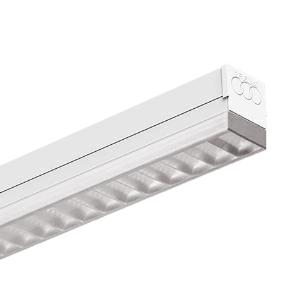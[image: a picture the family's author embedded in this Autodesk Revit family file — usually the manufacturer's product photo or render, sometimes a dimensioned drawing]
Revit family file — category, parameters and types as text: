
# Revit family: 3f_filippi_-_3f_linux_dr_ugr_3f_filippi_-_a20600_-_3f_linux_dr_2x22_led_dali_ugr_l1778
name_source: partatom
category: Lighting Fixtures
units: mm (PartAtom-declared; Revit-internal decimal feet)

## family parameters
Cut with Voids When Loaded = No
Host = Face
Light Source = No
Part Type = Normal
Room Calculation Point = No
Round Connector Dimension = Use Diameter
Shared = No

## types (1)
- 3F Filippi - 3F Linux DR UGR (1 x LED, 5361 lm, 49 W, 4000 K)
    Apparent Load = 49 VA
    Approval mark = CE
    CIE Flux Codes = 71 97 100 99 100
    Color Rendering = 80
    Color Temperature = 4000 K
    Control Gear = Electronic transformer
    Default Elevation = 1800 mm
    Description = Light unit for structure continues 3F Linux S.

ILLUMINOTECHNICAL
Luminous efficiency 100% (DLOR 99%, ULOR 1%).
Initial luminous flux of the luminaire 5361 lm.
Direct symmetric distribution.
Installation Interdistance Transv.D = 1.24 x hu - Long.D = 1.17 x hu.
Average luminance <3000 cd/m² for radial angles >65°.
Tabular UGR (CIE 117 - 4H-8H; S=0.25H; 70/50/20): RUG 17.8 - 19.
Beam angle: 87° - 90°.
Luminous efficacy 109 lm/W.
Lifetime (L93/B10): 30000 h. (tq+25°C)
Lifetime (L90/B10): 50000 h. (tq+25°C)
Lifetime (L85/B10): 80000 h. (tq+25°C)
Lifetime (L80/B10): 100000 h. (tq+25°C)
Sudden decreased luminous flux after 50000 hours: 0% (C0).
Photobiological safety in compliance with IEC/TR 62778: RG0 risk exempt, (IEC 62471).
In compliance with IEC/EN 62722-2-1 - IEC/EN 62717 standards.

SOURCE
2 linear LED modules 22W/840.
Energy efficiency class (UE 2019/2020 - UE 2019/2015): D.
CIE 13.3 Colour rendering index: CRI >80 (R9 <50%).
IES TM-30 Fidelity Index: Rf = 84 Rg = 95.
CCT nominal colour temperature 4000 K.
Colour initial tolerance (MacAdam): SDCM 3.

MECHANICAL
Light unit in hot-galvanised steel, painted in white polyester base with fixing springs and retractable safety hooks in stainless steel.
Rectangular screen in self-extinguishing polycarbonate, UV stabilised, transparent, with smooth outer surface.
Semi-specular aluminium internal louvre with prismatic methacrylate (PMMA) filter above the louvre blades for complete shielding of the louvre compartment.
Luminaire with limited surface temperature. - D - (EN 60598-2-24)
Dimensions: 1778x62 mm, height 81 mm. Weight 2.965 kg.
IP40 protection degree.
Mechanical strength to impacts IK06 (1 joule).
Glow-wire test resistance 850°C.

ELECTRICAL
Halogen Free DALI-2 DATI (Parts 251, 252, 253), PUSH-DIM, electronic wiring 230V-50/60Hz, power factor 0.95 at full load, THD <25%, constant output current, SELV, class I, 1 driver, 1 DALI addresse.
Power of the luminaire 49 W.
ENEC - CE.
SAFE FLICKER: PstLM=<1 and SVM=<0.4 (IEC TR 61547-1 and IEC TR 63158), to ensure a more comfortable and safe light.
Luminaire compliant with EN 60598-2-22 for power supply from a centralised emergency system CPSS (Central Power Supply System), not incorporated in the luminaire - high risk areas excluded. The default power and flux are 100% in AC and 15% in DC.
Ambient temperature from 0°C to +35°C.
Temperature class T6 max 85°C.
Connection to the structure with 3-pin plug with phase selection (H05Z-U Halogen Free cable section 0.5 mm² HT90).
Relative humidity UR: <85%.

INSTALLATION
Ceiling / Suspended / Wall.
All accessories dedicated to this product are available on the Catalog and on our website www.3F-Filippi.com.

STRUCTURE
Hot-galvanised wired structure, painted in polyester base white, obtained through rolling process.
Saline-mist resistance equal to 300hrs and damp resistance equal to 700hrs.
Through-wiring 5 or 7 poles with cables H07Z-U Halogen Free section 2.5 mm² HT90, with quick connecting terminal, irreversible, start / end and intermediate power towers.
Linear connecting element in hot galvanised steel already mounted on one end to form continuous channels, only L3556 structures.
A20017 - 3F Linux S 5P L3556, structure with through-wiring 5-pole.
A20019 - 3F Linux S 5P L1778, structure with through-wiring 5-pole.
A20024 - 3F Linux S 7P L3556, structure with through-wiring 7-pole.
A20026 - 3F Linux S 7P L1778, structure with through-wiring 7-pole.

APPLICATIONS
Suitable product for food production plants (HACCP), IFS (Food Version 6), BRC (GSFS Food Version 7).
In commercial environments, exhibition areas, shops and stores.

LIGHT MANAGEMENT
Recommended minimum setting: 10%.
The luminaire, equipped with (DALI-2 DATI) driver, can be controlled manually with 3F Easy Dim technology or automatically/manually with wired or wireless DALI/D2D control systems.
The D2D driver guarantees interoperability with other devices with the same certification by making the following information available:
Device Data (Part 251), Energy Report (Part 252), Diagnosis & Maintenance (Part 253).
In electrical systems without a regulation system (manual or automatic) and DALI bus, a suitable jumper must be made on the DA-DA terminals of the appliance.

WARNING
Luminaire designed for disposal/recycling at end-of-life.
Replaceable (LED only) light source by a professional. Replaceable control gear by a professional.
    Height = 81 mm
    Lamp = 1 x LED
    Lamp Light Flux = 5361 lm
    Lamp Power = 49 W
    Lamp count = 1
    Length = 1778 mm
    Lifetime = 50000 h
    Luminous efficacy = 109 lm/W
    Manufacturer = 3F Filippi
    ModVariant = No
    Model = 3F Filippi - A20600 - 3F Linux DR 2x22 LED DALI UGR L1778
    Mounting Place = Ceiling
    Mounting Type = Pendant
    Number of Poles = 1
    OnlyDefault = Yes
    Power Factor = 1
    Product Name = 3F Filippi - 3F Linux DR UGR
    Product group = pendant luminaire
    ProductGroupID = 9
    Protection Class = Protection class I
    Protection Degree = IP 40
    RLX_Detail_Level = 1
    RLX_Emergency_Light_Flux = 0 lm
    RLX_Emergency_Type = 0
    RLX_Emergency_Type_DB = No
    RlxData = <blob elided: 50949 chars, md5=39e6a370>
    Socket = socket
    Standby Power = 0 W
    System Light Flux = 5361 lm
    System Power = 49 W
    Type Comments = Product without accessories
    Type Image = 3ffilippi_3f_linux_dr_ugr.jpg
    URL = http://relux.com
    VarID = ---
    Voltage = 0 V
    Weight = 0.00 kg
    Width = 62 mm  [stored 0.203412 ft]

note: [stored X ft] marks values corroborated as IEEE doubles in the binary element streams (Revit-internal decimal feet)

## geometry (parser evidence)
native form markers: Blend x4, Sweep x9
no freeform markers — native parametric forms only
